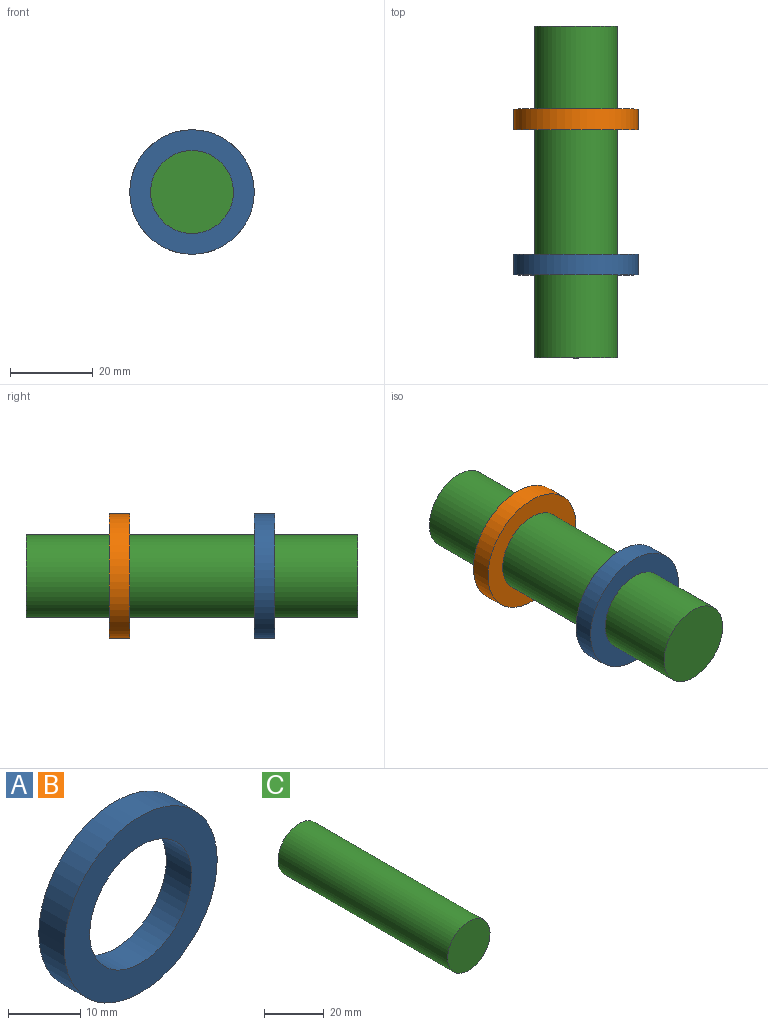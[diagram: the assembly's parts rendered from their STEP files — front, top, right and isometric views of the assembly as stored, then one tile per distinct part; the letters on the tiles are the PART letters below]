
ASSEMBLY  parts=3 mates=2
PART A: 4 faces, bbox 30x5x30 mm
  f0: cylinder r=15mm len=30mm, axis (0,1,0), area 471.2mm2, adj f1,f2
  f1: plane 30x30mm, normal (0,-1,0), area 392.7mm2, adj f0,f3
  f2: plane 30x30mm, normal (0,1,0), area 392.7mm2, adj f0,f3
  f3: cylinder r=10mm len=20mm, axis (0,1,0), area 314.2mm2, adj f1,f2
PART B: same geometry as A
PART C: 3 faces, bbox 20x80x20 mm
  f0: cylinder r=10mm len=80mm, axis (0,1,0), area 5026.5mm2, adj f1,f2
  f1: plane 20x20mm, normal (0,-1,0), area 314.2mm2, adj f0
  f2: plane 20x20mm, normal (0,1,0), area 314.2mm2, adj f0
PLACE A rot(axis=(1,0,0),180deg) t=(4.13,-20.9,12.31)mm
PLACE B t=(4.13,19.1,12.31)mm
PLACE C rot(axis=(1,0,0),180deg) t=(4.13,-40.9,12.31)mm
MATE fastened A.f3 <-> C.f0  axis (0,-1,0) through (4.13,-15.9,12.31)mm
MATE fastened C.f0 <-> B.f0  axis (0,-1,0) through (4.13,-0.9,12.31)mm
